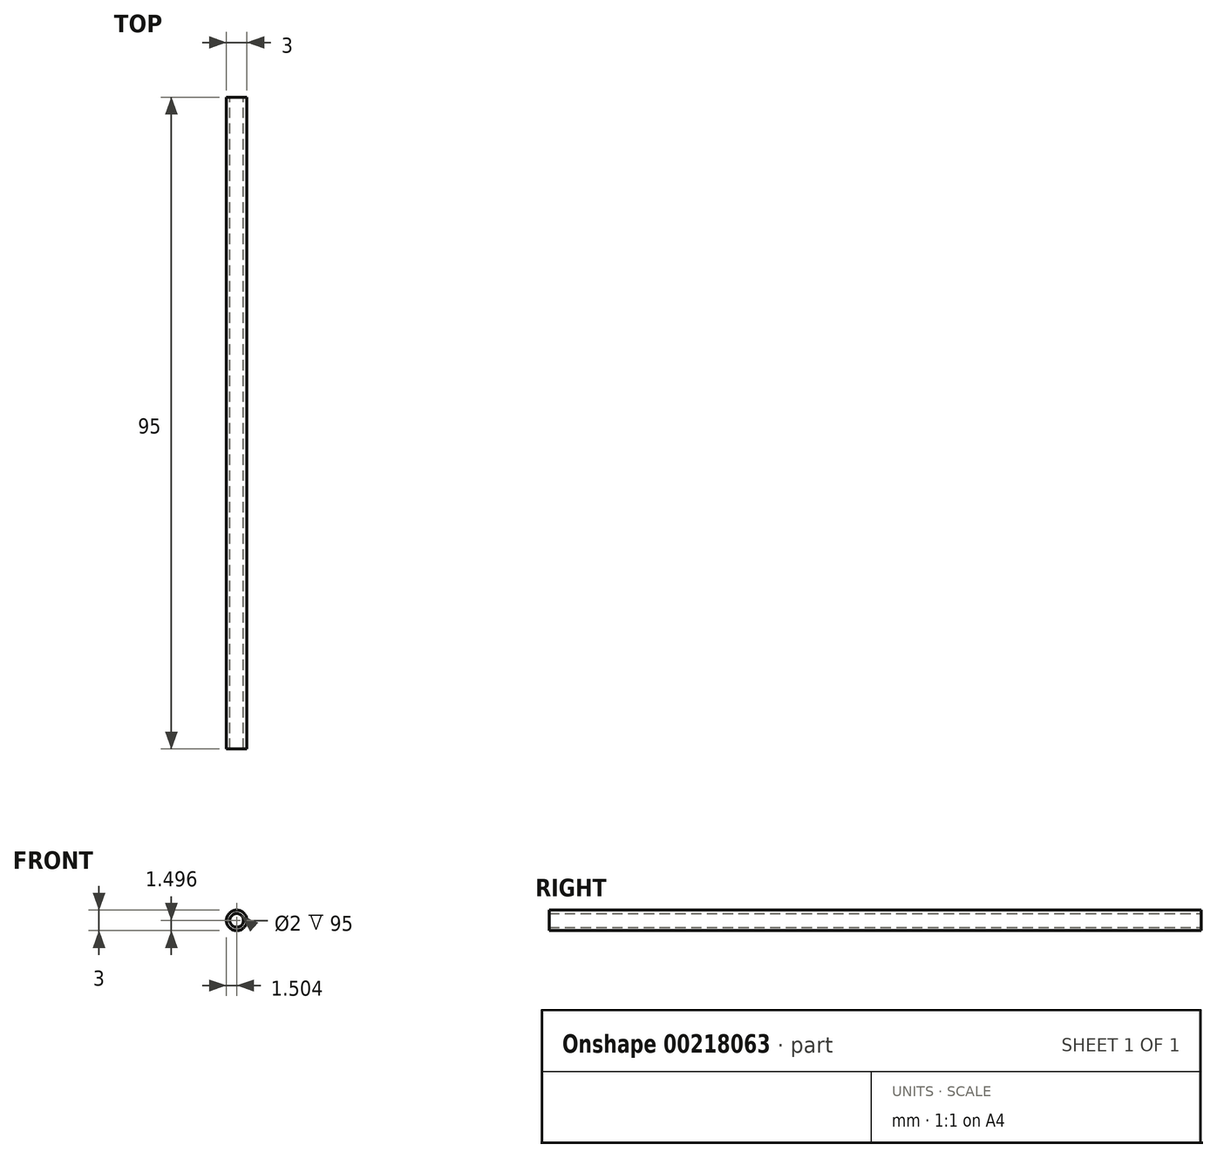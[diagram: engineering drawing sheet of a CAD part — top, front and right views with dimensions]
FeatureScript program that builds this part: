
annotation { "Feature Type Name" : "Feature", "Feature Type Description" : "" }
export const myFeature = defineFeature(function(context is Context, id is Id, definition is map)
    precondition{}
    {
        {
            var Q0;
            Q0=qCreatedBy(makeId("Front.planeOp"),FACE);
            var sketch = newSketch(context, id + "F0", { "sketchPlane" : qUnion([Q0])});
            skCircle(sketch, "E0", {"center": v(18.68, 12.5) * mm, "radius": 1.5 * mm});
            skCircle(sketch, "E1", {"center": v(18.68, 12.5) * mm, "radius": 1 * mm});
            skSolve(sketch);
        }
        {
            var Q0;
            Q0=makeQuery(id+"F0.imprint","IMPRINT",FACE,{"disambiguationData":[TD([[makeQuery(id+"F0.imprint","IMPRINT",EDGE,{"derivedFrom":sQuery(id+"F0.wireOp",EDGE,"E0")}),1.0]])]});
            extrude(context, id + "F1", {"entities" : qUnion([Q0]), "depth" : 95 * mm});
        }
    });
